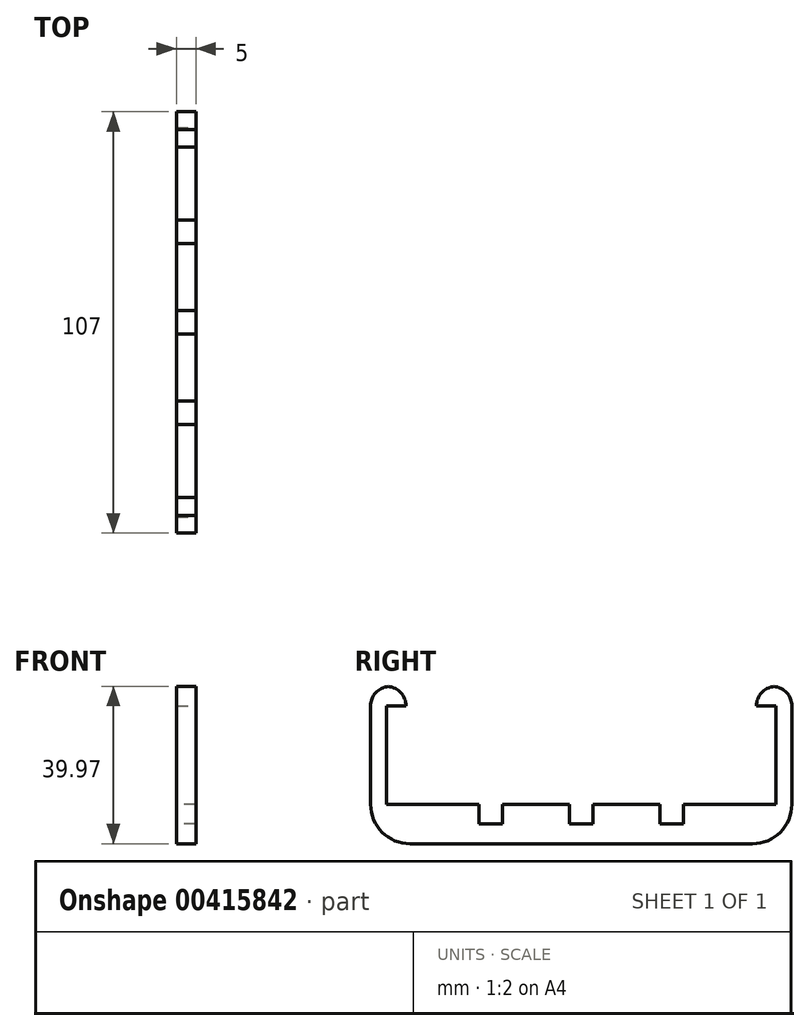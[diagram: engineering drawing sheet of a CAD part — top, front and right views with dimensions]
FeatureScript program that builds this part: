
annotation { "Feature Type Name" : "Feature", "Feature Type Description" : "" }
export const myFeature = defineFeature(function(context is Context, id is Id, definition is map)
    precondition{}
    {
        {
            var Q0;
            Q0=qCreatedBy(makeId("Top.planeOp"),FACE);
            var sketch = newSketch(context, id + "F0", { "sketchPlane" : qUnion([Q0])});
            skLineSegment(sketch, "E0.bottom", {"start": v(2.5, 53.5) * mm, "end": v(-2.5, 53.5) * mm});
            skLineSegment(sketch, "E0.top", {"start": v(2.5, -53.5) * mm, "end": v(-2.5, -53.5) * mm});
            skLineSegment(sketch, "E0.left", {"start": v(2.5, 53.5) * mm, "end": v(2.5, -53.5) * mm});
            skLineSegment(sketch, "E0.right", {"start": v(-2.5, 53.5) * mm, "end": v(-2.5, -53.5) * mm});
            skPoint(sketch, "E0.middle", {"position": v(0, 0) * mm});
            skSolve(sketch);
        }
        {
            var Q0;
            {var subQ0=sQuery(id+"F0.wireOp",EDGE,"E0.bottom");Q0=makeQuery(id+"F0.imprint","IMPRINT",FACE,{"disambiguationData":[TD([[makeQuery(id+"F0.imprint","IMPRINT",EDGE,{"derivedFrom":subQ0}),1.0]])]});}
            var Q1;
            {var subQ5=sQuery(id+"F0.wireOp",EDGE,"9zgWwLos-s7FM-WRk8-Seod-YjctP52RaN4v.left");Q1=makeQuery(id+"F0.imprint","IMPRINT",FACE,{"disambiguationData":[TD([[makeQuery(id+"F0.imprint","IMPRINT",EDGE,{"derivedFrom":subQ5}),-1.0]])]});}
            var Q2;
            {var subQ0=sQuery(id+"F0.wireOp",EDGE,"9zgWwLos-s7FM-WRk8-Seod-YjctP52RaN4v.bottom");var subQ1=sQuery(id+"F0.wireOp",EDGE,"E0.left");var subQ2=makeQuery(id+"F0.imprint","INTERSECT",VERTEX,{"derivedFrom":[subQ1,subQ0]});Q2=makeQuery(id+"F0.imprint","IMPRINT",FACE,{"disambiguationData":[TD([[makeQuery(id+"F0.imprint","IMPRINT",EDGE,{"disambiguationData":[TD([[subQ2,-1.0]])],"derivedFrom":subQ1}),-1.0]])]});}
            var Q3;
            {var subQ5=sQuery(id+"F0.wireOp",EDGE,"9zgWwLos-s7FM-WRk8-Seod-YjctP52RaN4v.right");Q3=makeQuery(id+"F0.imprint","IMPRINT",FACE,{"disambiguationData":[TD([[makeQuery(id+"F0.imprint","IMPRINT",EDGE,{"derivedFrom":subQ5}),1.0]])]});}
            var Q4;
            {var subQ0=sQuery(id+"F0.wireOp",EDGE,"E0.top");Q4=makeQuery(id+"F0.imprint","IMPRINT",FACE,{"disambiguationData":[TD([[makeQuery(id+"F0.imprint","IMPRINT",EDGE,{"derivedFrom":subQ0}),-1.0]])]});}
            extrude(context, id + "F1", {"entities" : qUnion([Q0, Q1, Q2, Q3, Q4]), "depth" : 10 * mm});
        }
        {
            var Q0;
            Q0=makeQuery(id+"F1.opExtrude","CAP_FACE",FACE,{"disambiguationData":[OSD([sQuery(id+"F0.wireOp",EDGE,"E0.bottom"),sQuery(id+"F0.wireOp",EDGE,"E0.top"),sQuery(id+"F0.wireOp",EDGE,"E0.left"),sQuery(id+"F0.wireOp",EDGE,"E0.right"),sQuery(id+"F0.wireOp",EDGE,"9zgWwLos-s7FM-WRk8-Seod-YjctP52RaN4v.bottom"),sQuery(id+"F0.wireOp",EDGE,"9zgWwLos-s7FM-WRk8-Seod-YjctP52RaN4v.top"),sQuery(id+"F0.wireOp",EDGE,"9zgWwLos-s7FM-WRk8-Seod-YjctP52RaN4v.left"),sQuery(id+"F0.wireOp",EDGE,"9zgWwLos-s7FM-WRk8-Seod-YjctP52RaN4v.right")])],"isStart":false});
            var sketch = newSketch(context, id + "F2", { "sketchPlane" : qUnion([Q0])});
            skLineSegment(sketch, "E1.bottom", {"start": v(-2.5, 53.5) * mm, "end": v(2.5, 53.5) * mm});
            skLineSegment(sketch, "E1.top", {"start": v(-2.5, 49.5) * mm, "end": v(2.5, 49.5) * mm});
            skLineSegment(sketch, "E1.left", {"start": v(-2.5, 53.5) * mm, "end": v(-2.5, 49.5) * mm});
            skLineSegment(sketch, "E1.right", {"start": v(2.5, 53.5) * mm, "end": v(2.5, 49.5) * mm});
            skLineSegment(sketch, "E2.MirrorCS", {"start": v(2.5, -53.5) * mm, "end": v(2.5, -49.5) * mm});
            skLineSegment(sketch, "E3.MirrorCS", {"start": v(-2.5, -53.5) * mm, "end": v(2.5, -53.5) * mm});
            skLineSegment(sketch, "E4.MirrorCS", {"start": v(-2.5, -49.5) * mm, "end": v(2.5, -49.5) * mm});
            skLineSegment(sketch, "E5.MirrorCS", {"start": v(-2.5, -53.5) * mm, "end": v(-2.5, -49.5) * mm});
            skSolve(sketch);
        }
        {
            var Q0;
            Q0=makeQuery(id+"F1.opExtrude","CAP_FACE",FACE,{"disambiguationData":[OSD([sQuery(id+"F0.wireOp",EDGE,"E0.bottom"),sQuery(id+"F0.wireOp",EDGE,"E0.top"),sQuery(id+"F0.wireOp",EDGE,"E0.left"),sQuery(id+"F0.wireOp",EDGE,"E0.right"),sQuery(id+"F0.wireOp",EDGE,"9zgWwLos-s7FM-WRk8-Seod-YjctP52RaN4v.bottom"),sQuery(id+"F0.wireOp",EDGE,"9zgWwLos-s7FM-WRk8-Seod-YjctP52RaN4v.top"),sQuery(id+"F0.wireOp",EDGE,"9zgWwLos-s7FM-WRk8-Seod-YjctP52RaN4v.left"),sQuery(id+"F0.wireOp",EDGE,"9zgWwLos-s7FM-WRk8-Seod-YjctP52RaN4v.right")])],"isStart":false});
            var sketch = newSketch(context, id + "F3", { "sketchPlane" : qUnion([Q0])});
            skLineSegment(sketch, "E6.bottom", {"start": v(2.5, 26) * mm, "end": v(-2.5, 26) * mm});
            skLineSegment(sketch, "E6.top", {"start": v(2.5, 20) * mm, "end": v(-2.5, 20) * mm});
            skLineSegment(sketch, "E6.left", {"start": v(2.5, 26) * mm, "end": v(2.5, 20) * mm});
            skLineSegment(sketch, "E6.right", {"start": v(-2.5, 26) * mm, "end": v(-2.5, 20) * mm});
            skPoint(sketch, "E6.middle", {"position": v(0, 23) * mm});
            skLineSegment(sketch, "E7.MirrorCS", {"start": v(2.5, -20) * mm, "end": v(-2.5, -20) * mm});
            skLineSegment(sketch, "E8.MirrorCS", {"start": v(-2.5, -26) * mm, "end": v(-2.5, -20) * mm});
            skLineSegment(sketch, "E9.MirrorCS", {"start": v(2.5, -26) * mm, "end": v(-2.5, -26) * mm});
            skLineSegment(sketch, "E10.MirrorCS", {"start": v(2.5, -26) * mm, "end": v(2.5, -20) * mm});
            skSolve(sketch);
        }
        {
            var Q0;
            Q0=makeQuery(id+"F3.imprint","IMPRINT",FACE,{"disambiguationData":[TD([[makeQuery(id+"F3.imprint","IMPRINT",EDGE,{"derivedFrom":sQuery(id+"F3.wireOp",EDGE,"E6.bottom")}),1.0]])]});
            extrude(context, id + "F4", {"entities" : qUnion([Q0]), "operationType" : NewBodyOperationType.REMOVE, "oppositeDirection" : true, "depth" : 5 * mm});
        }
        {
            var Q0;
            Q0 = qSketchRegion(id + "F3", true);
            extrude(context, id + "F5", {"entities" : qUnion([Q0]), "operationType" : NewBodyOperationType.REMOVE, "oppositeDirection" : true, "depth" : 5 * mm});
        }
        {
            var Q0;
            Q0=makeQuery(id+"F1.opExtrude","CAP_EDGE",EDGE,{"disambiguationData":[OSD([sQuery(id+"F0.wireOp",EDGE,"E0.top")])],"isStart":true});
            var Q1;
            Q1=makeQuery(id+"F1.opExtrude","CAP_EDGE",EDGE,{"disambiguationData":[OSD([sQuery(id+"F0.wireOp",EDGE,"E0.bottom")])],"isStart":true});
            fillet(context, id + "F6", {"entities" : qUnion([Q0, Q1]), "radius" : 10 * mm, "tangentPropagation" : true, "allowEdgeOverflow" : false});
        }
        {
            var Q0;
            Q0=makeQuery(id+"F2.imprint","IMPRINT",FACE,{"disambiguationData":[TD([[makeQuery(id+"F2.imprint","IMPRINT",EDGE,{"derivedFrom":sQuery(id+"F2.wireOp",EDGE,"E1.bottom")}),1.0]])]});
            extrude(context, id + "F7", {"entities" : qUnion([Q0]), "operationType" : NewBodyOperationType.ADD, "depth" : 30 * mm});
        }
        {
            var Q0;
            Q0 = qSketchRegion(id + "F2", true);
            extrude(context, id + "F8", {"entities" : qUnion([Q0]), "operationType" : NewBodyOperationType.ADD, "depth" : 30 * mm});
        }
        {
            var Q0;
            Q0=makeQuery(id+"F8.opExtrude","SWEPT_FACE",FACE,{"disambiguationData":[OSD([sQuery(id+"F2.wireOp",EDGE,"E4.MirrorCS")])]});
            var sketch = newSketch(context, id + "F9", { "sketchPlane" : qUnion([Q0])});
            skLineSegment(sketch, "E11.bottom", {"start": v(-2.5, 40) * mm, "end": v(2.5, 40) * mm});
            skLineSegment(sketch, "E11.top", {"start": v(-2.5, 35) * mm, "end": v(2.5, 35) * mm});
            skLineSegment(sketch, "E11.left", {"start": v(-2.5, 40) * mm, "end": v(-2.5, 35) * mm});
            skLineSegment(sketch, "E11.right", {"start": v(2.5, 40) * mm, "end": v(2.5, 35) * mm});
            skSolve(sketch);
        }
        {
            var Q0;
            Q0 = qSketchRegion(id + "F9", true);
            extrude(context, id + "F10", {"entities" : qUnion([Q0]), "operationType" : NewBodyOperationType.ADD, "depth" : 5 * mm});
        }
        {
            var Q0;
            Q0=makeQuery(id+"F7.opExtrude","SWEPT_FACE",FACE,{"disambiguationData":[OSD([sQuery(id+"F2.wireOp",EDGE,"E1.top")])]});
            var sketch = newSketch(context, id + "F11", { "sketchPlane" : qUnion([Q0])});
            skLineSegment(sketch, "E12.bottom", {"start": v(-2.5, 40) * mm, "end": v(2.5, 40) * mm});
            skLineSegment(sketch, "E12.top", {"start": v(-2.5, 35) * mm, "end": v(2.5, 35) * mm});
            skLineSegment(sketch, "E12.left", {"start": v(-2.5, 40) * mm, "end": v(-2.5, 35) * mm});
            skLineSegment(sketch, "E12.right", {"start": v(2.5, 40) * mm, "end": v(2.5, 35) * mm});
            skSolve(sketch);
        }
        {
            var Q0;
            Q0 = qSketchRegion(id + "F11", true);
            extrude(context, id + "F12", {"entities" : qUnion([Q0]), "operationType" : NewBodyOperationType.ADD, "depth" : 5 * mm});
        }
        {
            var Q0;
            Q0=makeQuery(id+"F8.opExtrude","CAP_EDGE",EDGE,{"disambiguationData":[OSD([sQuery(id+"F2.wireOp",EDGE,"E3.MirrorCS")])],"isStart":false});
            var Q1;
            Q1=makeQuery(id+"F7.opExtrude","CAP_EDGE",EDGE,{"disambiguationData":[OSD([sQuery(id+"F2.wireOp",EDGE,"E1.bottom")])],"isStart":false});
            var Q2;
            Q2=makeQuery(id+"F12.opExtrude","CAP_EDGE",EDGE,{"disambiguationData":[OSD([sQuery(id+"F11.wireOp",EDGE,"E12.bottom")])],"isStart":false});
            var Q3;
            Q3=makeQuery(id+"F10.opExtrude","CAP_EDGE",EDGE,{"disambiguationData":[OSD([sQuery(id+"F9.wireOp",EDGE,"E11.bottom")])],"isStart":false});
            fillet(context, id + "F13", {"entities" : qUnion([Q0, Q1, Q2, Q3]), "radius" : 5 * mm, "tangentPropagation" : true, "allowEdgeOverflow" : false});
        }
        {
            var Q0;
            {var subQ0=sQuery(id+"F0.wireOp",EDGE,"E0.left");var subQ2=sQuery(id+"F0.wireOp",EDGE,"E0.right");var subQ4=makeQuery(id+"F4.opExtrude","SWEPT_FACE",FACE,{"disambiguationData":[OSD([sQuery(id+"F3.wireOp",EDGE,"E6.top")])]});var subQ5=sQuery(id+"F0.wireOp",EDGE,"E0.top");Q0=makeQuery(id+"F5.boolean.opBoolean","SPLIT",FACE,{"disambiguationData":[TD([makeQuery(id+"F4.boolean.opBoolean","COPY",FACE,{"derivedFrom":subQ4})])],"derivedFrom":makeQuery(id+"F4.boolean.opBoolean","SPLIT",FACE,{"disambiguationData":[TD([makeQuery(id+"F1.opExtrude","SWEPT_FACE",FACE,{"disambiguationData":[OSD([subQ5])]})])],"derivedFrom":makeQuery(id+"F1.opExtrude","CAP_FACE",FACE,{"disambiguationData":[OSD([sQuery(id+"F0.wireOp",EDGE,"E0.bottom"),subQ5,subQ0,subQ2])],"isStart":false})})});}
            var sketch = newSketch(context, id + "F14", { "sketchPlane" : qUnion([Q0])});
            skLineSegment(sketch, "E13.bottom", {"start": v(2.5, 3) * mm, "end": v(-2.5, 3) * mm});
            skLineSegment(sketch, "E13.top", {"start": v(2.5, -3) * mm, "end": v(-2.5, -3) * mm});
            skLineSegment(sketch, "E13.left", {"start": v(2.5, 3) * mm, "end": v(2.5, -3) * mm});
            skLineSegment(sketch, "E13.right", {"start": v(-2.5, 3) * mm, "end": v(-2.5, -3) * mm});
            skPoint(sketch, "E13.middle", {"position": v(0, 0) * mm});
            skSolve(sketch);
        }
        {
            var Q0;
            Q0=makeQuery(id+"F14.imprint","IMPRINT",FACE,{"disambiguationData":[TD([[makeQuery(id+"F14.imprint","IMPRINT",EDGE,{"derivedFrom":sQuery(id+"F14.wireOp",EDGE,"E13.bottom")}),1.0]])]});
            extrude(context, id + "F15", {"entities" : qUnion([Q0]), "operationType" : NewBodyOperationType.REMOVE, "oppositeDirection" : true, "depth" : 5 * mm});
        }
    });
